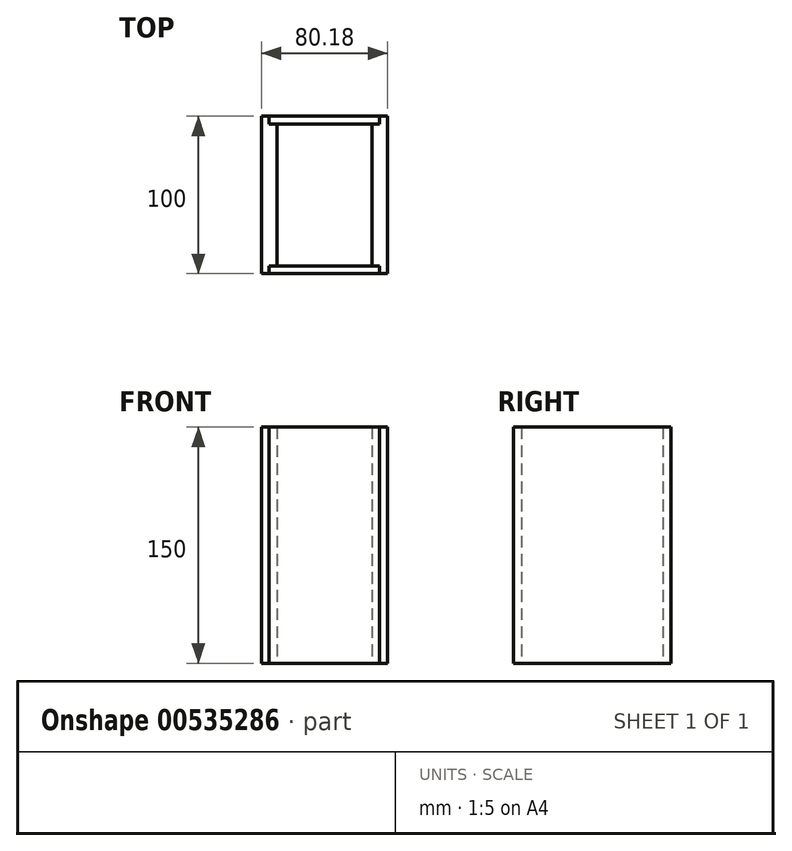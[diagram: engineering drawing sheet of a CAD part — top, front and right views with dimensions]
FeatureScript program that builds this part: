
annotation { "Feature Type Name" : "Feature", "Feature Type Description" : "" }
export const myFeature = defineFeature(function(context is Context, id is Id, definition is map)
    precondition{}
    {
        {
            var Q0;
            Q0=qCreatedBy(makeId("Top.planeOp"),FACE);
            var sketch = newSketch(context, id + "F0", { "sketchPlane" : qUnion([Q0])});
            skLineSegment(sketch, "E0", {"start": v(-40.1, 100) * mm, "end": v(-40.1, 0) * mm});
            skLineSegment(sketch, "E1", {"start": v(-40.1, 0) * mm, "end": v(-35.1, 0) * mm});
            skLineSegment(sketch, "E2", {"start": v(-35.1, 0) * mm, "end": v(-35.1, 5) * mm});
            skLineSegment(sketch, "E3", {"start": v(-35.1, 5) * mm, "end": v(-30.1, 5) * mm});
            skLineSegment(sketch, "E4", {"start": v(-30.1, 5) * mm, "end": v(-30.1, 95) * mm});
            skLineSegment(sketch, "E5", {"start": v(-30.1, 95) * mm, "end": v(-35.1, 95) * mm});
            skLineSegment(sketch, "E6", {"start": v(-35.1, 95) * mm, "end": v(-35.1, 100) * mm});
            skLineSegment(sketch, "E7", {"start": v(-35.1, 100) * mm, "end": v(-40.1, 100) * mm});
            skLineSegment(sketch, "E8.MirrorCS", {"start": v(30.1, 5) * mm, "end": v(30.1, 95) * mm});
            skLineSegment(sketch, "E9.MirrorCS", {"start": v(40.1, 100) * mm, "end": v(40.1, 0) * mm});
            skLineSegment(sketch, "E10.MirrorCS", {"start": v(40.1, 0) * mm, "end": v(35.1, 0) * mm});
            skLineSegment(sketch, "E11.MirrorCS", {"start": v(35.1, 100) * mm, "end": v(40.1, 100) * mm});
            skLineSegment(sketch, "E12.MirrorCS", {"start": v(35.1, 95) * mm, "end": v(35.1, 100) * mm});
            skLineSegment(sketch, "E13.MirrorCS", {"start": v(35.1, 0) * mm, "end": v(35.1, 5) * mm});
            skLineSegment(sketch, "E14.MirrorCS", {"start": v(35.1, 5) * mm, "end": v(30.1, 5) * mm});
            skLineSegment(sketch, "E15.MirrorCS", {"start": v(30.1, 95) * mm, "end": v(35.1, 95) * mm});
            skLineSegment(sketch, "E16.left", {"start": v(-35.1, 100) * mm, "end": v(-35.1, 95) * mm});
            skLineSegment(sketch, "E16.right", {"start": v(35.1, 100) * mm, "end": v(35.1, 95) * mm});
            skLineSegment(sketch, "E17.left", {"start": v(-35.1, 5) * mm, "end": v(-35.1, 0) * mm});
            skLineSegment(sketch, "E17.right", {"start": v(35.1, 5) * mm, "end": v(35.1, 0) * mm});
            skLineSegment(sketch, "E18.bottom", {"start": v(-35.1, 100) * mm, "end": v(35.1, 100) * mm});
            skLineSegment(sketch, "E18.top", {"start": v(-35.1, 95) * mm, "end": v(35.1, 95) * mm});
            skLineSegment(sketch, "E19.bottom", {"start": v(35.1, 0) * mm, "end": v(-35.1, 0) * mm});
            skLineSegment(sketch, "E19.top", {"start": v(35.1, 5) * mm, "end": v(-35.1, 5) * mm});
            skSolve(sketch);
        }
        {
            var Q0;
            Q0=makeQuery(id+"F0.imprint","IMPRINT",FACE,{"disambiguationData":[TD([[makeQuery(id+"F0.imprint","IMPRINT",EDGE,{"derivedFrom":sQuery(id+"F0.wireOp",EDGE,"E0")}),1.0]])]});
            var Q1;
            {var subQ1=sQuery(id+"F0.wireOp",EDGE,"E8.MirrorCS");Q1=makeQuery(id+"F0.imprint","IMPRINT",FACE,{"disambiguationData":[TD([[makeQuery(id+"F0.imprint","IMPRINT",EDGE,{"derivedFrom":subQ1}),-1.0]])]});}
            extrude(context, id + "F1", {"entities" : qUnion([Q0, Q1]), "depth" : 150 * mm, "offsetDistance" : 25 * mm});
        }
        {
            var Q0;
            {var subQ7=sQuery(id+"F0.wireOp",EDGE,"E18.bottom");Q0=makeQuery(id+"F0.imprint","IMPRINT",FACE,{"disambiguationData":[TD([[makeQuery(id+"F0.imprint","IMPRINT",EDGE,{"derivedFrom":subQ7}),-1.0]])]});}
            var Q1;
            Q1=makeQuery(id+"F0.imprint","IMPRINT",FACE,{"disambiguationData":[TD([[makeQuery(id+"F0.imprint","IMPRINT",EDGE,{"derivedFrom":sQuery(id+"F0.wireOp",EDGE,"E19.bottom")}),-1.0]])]});
            extrude(context, id + "F2", {"entities" : qUnion([Q0, Q1]), "depth" : 150 * mm, "offsetDistance" : 25 * mm});
        }
    });
